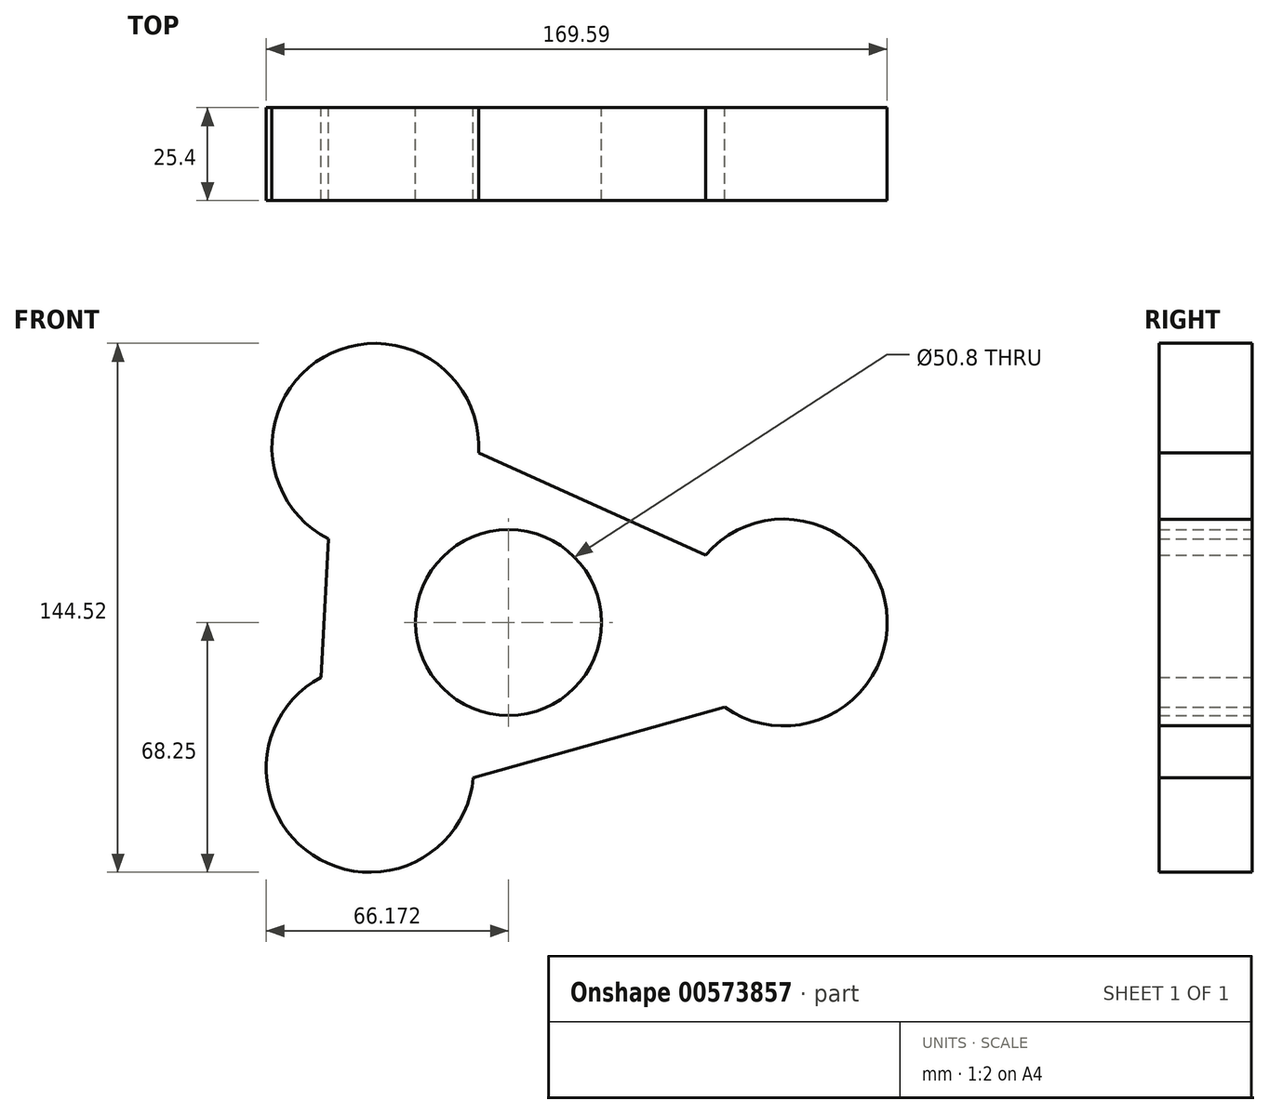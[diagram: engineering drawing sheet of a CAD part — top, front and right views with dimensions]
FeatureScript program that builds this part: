
annotation { "Feature Type Name" : "Feature", "Feature Type Description" : "" }
export const myFeature = defineFeature(function(context is Context, id is Id, definition is map)
    precondition{}
    {
        {
            var Q0;
            Q0=qCreatedBy(makeId("Front.planeOp"),FACE);
            var sketch = newSketch(context, id + "F0", { "sketchPlane" : qUnion([Q0])});
            skCircle(sketch, "E0", {"center": v(-54.66, 48.02) * mm, "radius": 28.25 * mm});
            skCircle(sketch, "E1", {"center": v(56.87, 0) * mm, "radius": 28.25 * mm});
            skLineSegment(sketch, "E2", {"start": v(-33.18, 29.68) * mm, "end": v(28.69, 1.91) * mm});
            skLineSegment(sketch, "E3", {"start": v(-26.46, 46.4) * mm, "end": v(35.5, 18.46) * mm});
            skCircle(sketch, "E4", {"center": v(-56.14, -39.91) * mm, "radius": 28.34 * mm});
            skLineSegment(sketch, "E5", {"start": v(30.63, -10.45) * mm, "end": v(-31.31, -26.24) * mm});
            skLineSegment(sketch, "E6", {"start": v(-27.91, -42.47) * mm, "end": v(40.72, -23.17) * mm});
            skLineSegment(sketch, "E7", {"start": v(-69.51, -14.93) * mm, "end": v(-67.44, 22.83) * mm});
            skSolve(sketch);
        }
        {
            var Q0;
            {var subQ0=sQuery(id+"F0.wireOp",EDGE,"E4");var subQ1=makeQuery(id+"F0.imprint","INTERSECT",VERTEX,{"derivedFrom":[subQ0,sQuery(id+"F0.wireOp",EDGE,"E5")]});Q0=makeQuery(id+"F0.imprint","IMPRINT",FACE,{"disambiguationData":[TD([[makeQuery(id+"F0.imprint","IMPRINT",EDGE,{"disambiguationData":[TD([[subQ1,-1.0]])],"derivedFrom":subQ0}),1.0]])]});}
            var Q1;
            {var subQ0=sQuery(id+"F0.wireOp",EDGE,"E0");var subQ1=makeQuery(id+"F0.imprint","INTERSECT",VERTEX,{"derivedFrom":[subQ0,sQuery(id+"F0.wireOp",EDGE,"E2")]});Q1=makeQuery(id+"F0.imprint","IMPRINT",FACE,{"disambiguationData":[TD([[makeQuery(id+"F0.imprint","IMPRINT",EDGE,{"disambiguationData":[TD([[subQ1,1.0]])],"derivedFrom":subQ0}),1.0]])]});}
            var Q2;
            {var subQ0=sQuery(id+"F0.wireOp",EDGE,"E2");Q2=makeQuery(id+"F0.imprint","IMPRINT",FACE,{"disambiguationData":[TD([[makeQuery(id+"F0.imprint","IMPRINT",EDGE,{"derivedFrom":subQ0}),-1.0]])]});}
            var Q3;
            {var subQ0=sQuery(id+"F0.wireOp",EDGE,"E5");Q3=makeQuery(id+"F0.imprint","IMPRINT",FACE,{"disambiguationData":[TD([[makeQuery(id+"F0.imprint","IMPRINT",EDGE,{"derivedFrom":subQ0}),1.0]])]});}
            var Q4;
            {var subQ0=sQuery(id+"F0.wireOp",EDGE,"E1");var subQ1=makeQuery(id+"F0.imprint","INTERSECT",VERTEX,{"derivedFrom":[subQ0,sQuery(id+"F0.wireOp",EDGE,"E2")]});Q4=makeQuery(id+"F0.imprint","IMPRINT",FACE,{"disambiguationData":[TD([[makeQuery(id+"F0.imprint","IMPRINT",EDGE,{"disambiguationData":[TD([[subQ1,1.0]])],"derivedFrom":subQ0}),1.0]])]});}
            var Q5;
            {var subQ0=sQuery(id+"F0.wireOp",EDGE,"E2");Q5=makeQuery(id+"F0.imprint","IMPRINT",FACE,{"disambiguationData":[TD([[makeQuery(id+"F0.imprint","IMPRINT",EDGE,{"derivedFrom":subQ0}),1.0]])]});}
            extrude(context, id + "F1", {"entities" : qUnion([Q0, Q1, Q2, Q3, Q4, Q5]), "depth" : 25.4 * mm, "offsetDistance" : 25.4 * mm});
        }
        {
            var Q0;
            Q0=qCreatedBy(makeId("Front.planeOp"),FACE);
            var sketch = newSketch(context, id + "F2", { "sketchPlane" : qUnion([Q0])});
            skCircle(sketch, "E8", {"center": v(-18.3, 0) * mm, "radius": 28.88 * mm});
            skSolve(sketch);
        }
        {
            var Q0;
            Q0=sQuery(id+"F2.wireOp",VERTEX,"E8.center");
            var Q1;
            Q1=makeQuery(id+"F1.opExtrude","SWEPT_BODY",BODY,{"disambiguationData":[OSD([sQuery(id+"F0.wireOp",EDGE,"E0"),sQuery(id+"F0.wireOp",EDGE,"E1"),sQuery(id+"F0.wireOp",EDGE,"E3"),sQuery(id+"F0.wireOp",EDGE,"E4"),sQuery(id+"F0.wireOp",EDGE,"E6"),sQuery(id+"F0.wireOp",EDGE,"E7")])]});
            hole(context, id + "F3", {"style" : HoleStyle.SIMPLE, "endStyle" : HoleEndStyle.THROUGH, "oppositeDirection" : true, "holeDiameter" : 50.8 * mm, "majorDiameter" : 6.35 * mm, "isTappedThrough" : true, "tappedDepth" : 12.7 * mm, "tapClearance" : 3, "locations" : qUnion([Q0]), "scope" : qUnion([Q1])});
        }
    });
